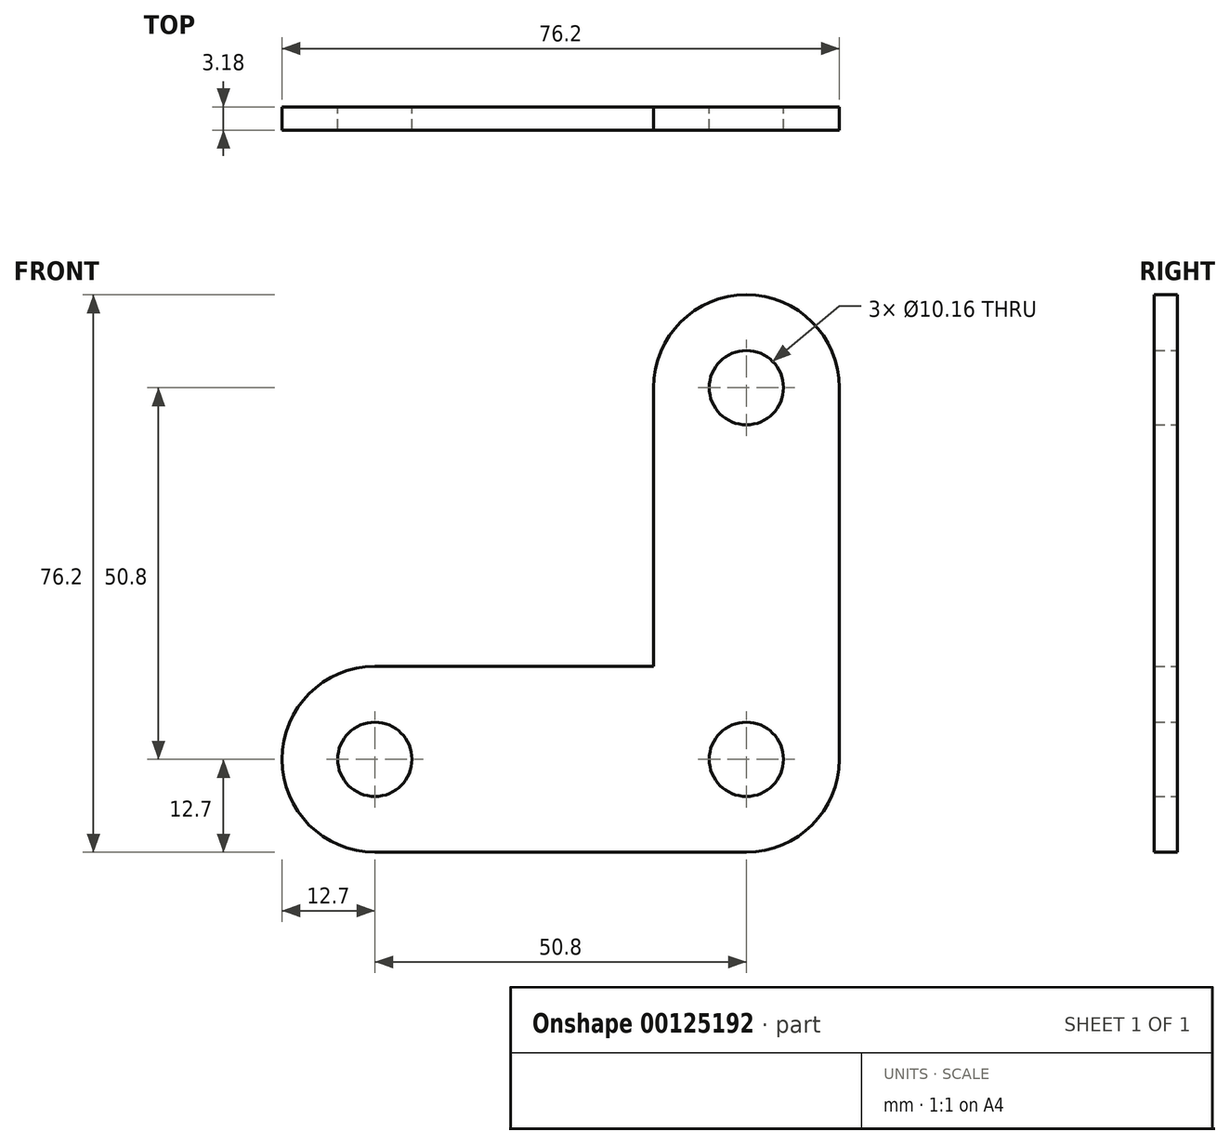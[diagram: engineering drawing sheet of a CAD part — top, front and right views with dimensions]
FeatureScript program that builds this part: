
annotation { "Feature Type Name" : "Feature", "Feature Type Description" : "" }
export const myFeature = defineFeature(function(context is Context, id is Id, definition is map)
    precondition{}
    {
        {
            var Q0;
            Q0=qCreatedBy(makeId("Front.planeOp"),FACE);
            var sketch = newSketch(context, id + "F0", { "sketchPlane" : qUnion([Q0])});
            skLineSegment(sketch, "E0", {"start": v(0, 12.7) * mm, "end": v(0, 63.5) * mm});
            skLineSegment(sketch, "E1", {"start": v(-12.7, 76.2) * mm, "end": v(-12.7, 76.2) * mm});
            skLineSegment(sketch, "E2", {"start": v(-12.7, 0) * mm, "end": v(-63.5, 0) * mm});
            skLineSegment(sketch, "E3", {"start": v(-76.2, 12.7) * mm, "end": v(-76.2, 12.7) * mm});
            skLineSegment(sketch, "E4", {"start": v(-63.5, 25.4) * mm, "end": v(-25.4, 25.4) * mm});
            skLineSegment(sketch, "E5", {"start": v(-25.4, 25.4) * mm, "end": v(-25.4, 63.5) * mm});
            skPoint(sketch, "E6.visualSharp", {"position": v(-76.2, 25.4) * mm});
            skArc(sketch, "E6.filletArc", {"start": v(-63.5, 25.4) * mm, "mid": v(-72.48, 21.68) * mm, "end": v(-76.2, 12.7) * mm});
            skPoint(sketch, "E7.visualSharp", {"position": v(-76.2, 0) * mm});
            skArc(sketch, "E7.filletArc", {"start": v(-76.2, 12.7) * mm, "mid": v(-72.48, 3.72) * mm, "end": v(-63.5, 0) * mm});
            skPoint(sketch, "E8.visualSharp", {"position": v(-25.4, 76.2) * mm});
            skArc(sketch, "E8.filletArc", {"start": v(-12.7, 76.2) * mm, "mid": v(-21.68, 72.48) * mm, "end": v(-25.4, 63.5) * mm});
            skPoint(sketch, "E9.visualSharp", {"position": v(0, 76.2) * mm});
            skArc(sketch, "E9.filletArc", {"start": v(0, 63.5) * mm, "mid": v(-3.72, 72.48) * mm, "end": v(-12.7, 76.2) * mm});
            skCircle(sketch, "E10", {"center": v(-63.5, 12.7) * mm, "radius": 5.08 * mm});
            skCircle(sketch, "E11", {"center": v(-12.7, 63.5) * mm, "radius": 5.08 * mm});
            skCircle(sketch, "E12", {"center": v(-12.7, 12.7) * mm, "radius": 5.08 * mm});
            skPoint(sketch, "E13.visualSharp", {"position": v(0, 0) * mm});
            skArc(sketch, "E13.filletArc", {"start": v(-12.7, 0) * mm, "mid": v(-3.72, 3.72) * mm, "end": v(0, 12.7) * mm});
            skSolve(sketch);
        }
        {
            var Q0;
            Q0 = qSketchRegion(id + "F0", true);
            extrude(context, id + "F1", {"entities" : qUnion([Q0]), "depth" : 3.17 * mm});
        }
    });
